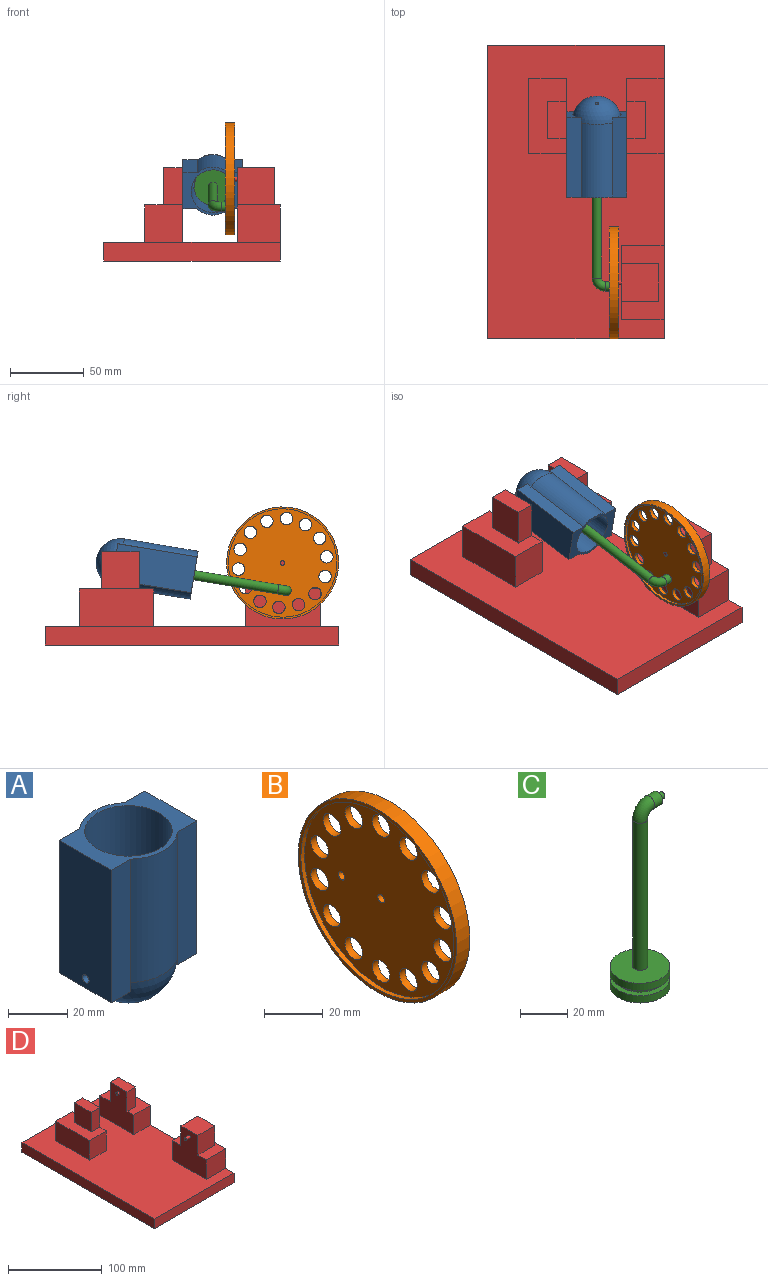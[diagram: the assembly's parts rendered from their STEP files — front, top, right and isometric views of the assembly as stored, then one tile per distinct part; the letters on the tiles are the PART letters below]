
ASSEMBLY  parts=4 mates=7
PART A: 22 faces, bbox 40.6x33x67.3 mm
  f0: sphere r=16.48mm, area 1697.5mm2, adj f2,f3,f6,f11,f20,f21
  f1: sphere r=14.7mm, area 1348.6mm2, adj f5,f20,f21
  f2: cylinder r=16.48mm len=50.8mm, axis (0,0,1), area 1242.1mm2, adj f0,f4,f8,f14
  f3: cylinder r=16.48mm len=50.8mm, axis (0,0,1), area 1178mm2, adj f0,f4,f7,f12
  f4: plane 40.63x32.95mm, normal (0,0,1), area 448.5mm2, adj f2,f3,f5,f7,f8,f9,f12,f13
  f5: cylinder r=14.7mm len=50.8mm, axis (0,0,1), area 4691.4mm2, adj f1,f4
  f6: cylinder r=16.48mm len=24.71mm, axis (0,0,1), area 106.5mm2, adj f0,f7,f8,f10
  f7: plane 54.61x9.65mm, normal (0,1,0), area 527.2mm2, adj f3,f4,f6,f9,f10
  f8: plane 54.61x9.18mm, normal (0,-1,0), area 501.4mm2, adj f2,f4,f6,f9,f10
  f9: plane 54.61x24.71mm, normal (1,0,0), area 1341.3mm2, adj f4,f7,f8,f10,f16
  f10: plane 24.71x9.65mm, normal (0,0,-1), area 137.2mm2, adj f6,f7,f8,f9
  f11: cylinder r=16.48mm len=24.71mm, axis (0,0,1), area 106.5mm2, adj f0,f12,f14,f15
  f12: plane 54.61x9.65mm, normal (0,1,0), area 527.2mm2, adj f3,f4,f11,f13,f15
  f13: plane 54.61x24.71mm, normal (-1,0,0), area 1341.4mm2, adj f4,f12,f14,f15,f18
  f14: plane 54.61x9.18mm, normal (0,-1,0), area 501.4mm2, adj f2,f4,f11,f13,f15
  f15: plane 24.71x9.65mm, normal (0,0,-1), area 137.2mm2, adj f11,f12,f13,f14
  f16: cylinder r=1.58mm len=3.17mm, axis (1,0,0), area 25.3mm2, adj f9,f17
  f17: plane 3.17x3.17mm, normal (1,0,0), area 7.9mm2, adj f16
  f18: cylinder r=1.58mm len=3.17mm, axis (-1,0,0), area 25.3mm2, adj f13,f19
  f19: plane 3.17x3.17mm, normal (-1,0,0), area 7.9mm2, adj f18
  f20: cylinder r=1.02mm len=4.01mm, axis (0,0,1), area 14.8mm2, adj f0,f1
  f21: cylinder r=1.02mm len=4.01mm, axis (0,0,1), area 14.8mm2, adj f0,f1
PART B: 23 faces, bbox 6.4x76.2x76.2 mm
  f0: plane 73.66x73.66mm, normal (1,0,0), area 3452.1mm2, adj f5,f7,f8,f9,f10,f11,f12,f13
  f1: plane 73.66x73.66mm, normal (-1,0,0), area 3452.1mm2, adj f6,f7,f8,f9,f10,f11,f12,f13
  f2: cylinder r=38.1mm len=76.2mm, axis (-1,0,0), area 1520.1mm2, adj f3,f4
  f3: plane 76.2x76.2mm, normal (1,0,0), area 299mm2, adj f2,f5
  f4: plane 76.2x76.2mm, normal (-1,0,0), area 299mm2, adj f2,f6
  f5: cylinder r=36.83mm len=73.66mm, axis (1,0,0), area 411.4mm2, adj f0,f3
  f6: cylinder r=36.83mm len=73.66mm, axis (-1,0,0), area 411.4mm2, adj f1,f4
  f7: cylinder r=1.59mm len=3.18mm, axis (1,0,0), area 27.9mm2, adj f0,f1
  f8: cylinder r=1.59mm len=3.18mm, axis (1,0,0), area 27.9mm2, adj f0,f1
  f9: cylinder r=4.25mm len=8.49mm, axis (1,0,0), area 74.6mm2, adj f0,f1
  f10: cylinder r=4.25mm len=8.49mm, axis (1,0,0), area 74.6mm2, adj f0,f1
  f11: cylinder r=4.25mm len=8.49mm, axis (1,0,0), area 74.6mm2, adj f0,f1
  f12: cylinder r=4.25mm len=8.49mm, axis (1,0,0), area 74.6mm2, adj f0,f1
  f13: cylinder r=4.25mm len=8.49mm, axis (1,0,0), area 74.6mm2, adj f0,f1
  f14: cylinder r=4.25mm len=8.49mm, axis (1,0,0), area 74.6mm2, adj f0,f1
  f15: cylinder r=4.25mm len=8.49mm, axis (1,0,0), area 74.6mm2, adj f0,f1
  f16: cylinder r=4.25mm len=8.49mm, axis (1,0,0), area 74.6mm2, adj f0,f1
  f17: cylinder r=4.25mm len=8.49mm, axis (1,0,0), area 74.6mm2, adj f0,f1
  f18: cylinder r=4.25mm len=8.49mm, axis (1,0,0), area 74.6mm2, adj f0,f1
  f19: cylinder r=4.25mm len=8.49mm, axis (1,0,0), area 74.6mm2, adj f0,f1
  f20: cylinder r=4.25mm len=8.49mm, axis (1,0,0), area 74.6mm2, adj f0,f1
  f21: cylinder r=4.25mm len=8.49mm, axis (1,0,0), area 74.6mm2, adj f0,f1
  f22: cylinder r=4.25mm len=8.49mm, axis (1,0,0), area 74.6mm2, adj f0,f1
PART C: 13 faces, bbox 26.1x25.4x96 mm
  f0: cylinder r=12.7mm len=25.4mm, axis (0,0,-1), area 304mm2, adj f1,f2
  f1: plane 25.4x25.4mm, normal (0,0,1), area 182.4mm2, adj f0,f3
  f2: plane 25.4x25.4mm, normal (0,0,-1), area 506.7mm2, adj f0
  f3: cylinder r=10.16mm len=20.32mm, axis (0,0,-1), area 162.1mm2, adj f1,f6
  f4: cylinder r=12.7mm len=25.4mm, axis (0,0,-1), area 304mm2, adj f5,f6
  f5: plane 25.4x25.4mm, normal (0,0,1), area 475mm2, adj f4,f7
  f6: plane 25.4x25.4mm, normal (0,0,-1), area 182.4mm2, adj f3,f4
  f7: cylinder r=3.17mm len=76.2mm, axis (0,0,-1), area 1520.1mm2, adj f5,f8
  f8: torus R=5.74mm, axis (0,-1,0), area 179.9mm2, adj f7,f9
  f9: cylinder r=3.17mm len=6.35mm, axis (-1,0,0), area 94.8mm2, adj f8,f10
  f10: plane 6.35x6.35mm, normal (1,0,0), area 23.8mm2, adj f9,f12
  f11: plane 3.18x3.18mm, normal (1,0,0), area 7.9mm2, adj f12
  f12: cylinder r=1.59mm len=3.18mm, axis (-1,0,0), area 28.6mm2, adj f10,f11
PART D: 37 faces, bbox 119.7x199.5x63.5 mm
  f0: plane 50.8x29.11mm, normal (0,0,1), area 833.5mm2, adj f7,f28,f29,f30,f31,f32,f34
  f1: plane 199.45x119.74mm, normal (0,0,1), area 19823.5mm2, adj f4,f5,f6,f7,f9,f10,f11,f12
  f2: plane 50.8x25.4mm, normal (0,0,1), area 967.7mm2, adj f7,f9,f10,f11,f20,f21,f22
  f3: plane 50.8x25.4mm, normal (0,0,1), area 967.7mm2, adj f12,f13,f14,f15,f16,f17,f18
  f4: plane 119.74x12.7mm, normal (0,1,0), area 1520.7mm2, adj f1,f5,f7,f8
  f5: plane 199.45x12.7mm, normal (-1,0,0), area 2533mm2, adj f1,f4,f6,f8
  f6: plane 119.74x12.7mm, normal (0,-1,0), area 1520.7mm2, adj f1,f5,f7,f8
  f7: plane 199.45x38.1mm, normal (1,0,0), area 5113.7mm2, adj f0,f1,f2,f4,f6,f8,f9,f11
  f8: plane 199.45x119.74mm, normal (0,0,-1), area 23882.8mm2, adj f4,f5,f6,f7
  f9: plane 25.4x25.4mm, normal (0,1,0), area 645.2mm2, adj f1,f2,f7,f10
  f10: plane 50.8x50.8mm, normal (-1,0,0), area 1927.6mm2, adj f1,f2,f9,f11,f20,f21,f23,f26
  f11: plane 25.4x25.4mm, normal (0,-1,0), area 645.2mm2, adj f1,f2,f7,f10
  f12: plane 25.4x25.4mm, normal (0,1,0), area 645.2mm2, adj f1,f3,f13,f15
  f13: plane 50.8x25.4mm, normal (-1,0,0), area 1290.3mm2, adj f1,f3,f12,f14
  f14: plane 25.4x25.4mm, normal (0,-1,0), area 645.2mm2, adj f1,f3,f13,f15
  f15: plane 50.8x50.8mm, normal (1,0,0), area 1927.6mm2, adj f1,f3,f12,f14,f16,f18,f19,f24
  f16: plane 25.4x12.7mm, normal (0,1,0), area 322.6mm2, adj f3,f15,f17,f19
  f17: plane 25.4x25.4mm, normal (-1,0,0), area 645.2mm2, adj f3,f16,f18,f19
  f18: plane 25.4x12.7mm, normal (0,-1,0), area 322.6mm2, adj f3,f15,f17,f19
  f19: plane 25.4x12.7mm, normal (0,0,1), area 322.6mm2, adj f15,f16,f17,f18
  f20: plane 25.4x12.7mm, normal (0,1,0), area 322.6mm2, adj f2,f10,f22,f23
  f21: plane 25.4x12.7mm, normal (0,-1,0), area 322.6mm2, adj f2,f10,f22,f23
  f22: plane 25.4x25.4mm, normal (1,0,0), area 645.2mm2, adj f2,f20,f21,f23
  f23: plane 25.4x12.7mm, normal (0,0,1), area 322.6mm2, adj f10,f20,f21,f22
  f24: cylinder r=1.59mm len=3.18mm, axis (-1,0,0), area 25.3mm2, adj f15,f25
  f25: plane 3.18x3.18mm, normal (1,0,0), area 7.9mm2, adj f24
  f26: cylinder r=1.59mm len=3.18mm, axis (1,0,0), area 25.3mm2, adj f10,f27
  f27: plane 3.18x3.18mm, normal (-1,0,0), area 7.9mm2, adj f26
  f28: plane 29.11x25.4mm, normal (0,1,0), area 739.3mm2, adj f0,f1,f7,f34
  f29: plane 29.11x25.4mm, normal (0,-1,0), area 739.3mm2, adj f0,f1,f7,f34
  f30: plane 25.4x25.4mm, normal (0,1,0), area 645.2mm2, adj f0,f32,f33,f34
  f31: plane 25.4x25.4mm, normal (0,-1,0), area 645.2mm2, adj f0,f32,f33,f34
  f32: plane 25.4x25.4mm, normal (1,0,0), area 645.2mm2, adj f0,f30,f31,f33
  f33: plane 25.4x25.4mm, normal (0,0,1), area 645.2mm2, adj f30,f31,f32,f34
  f34: plane 50.8x50.8mm, normal (-1,0,0), area 1927.6mm2, adj f0,f1,f28,f29,f30,f31,f33,f35
  f35: cylinder r=1.59mm len=6.35mm, axis (1,0,0), area 63.3mm2, adj f34,f36
  f36: plane 3.18x3.18mm, normal (-1,0,0), area 7.9mm2, adj f35
PLACE A rot(axis=(1,0,0),99.5deg) t=(4.73,-42.98,55.39)mm
PLACE B rot(axis=(-1,0,0),98deg) t=(13.21,-153.28,55.3)mm
PLACE C rot(axis=(1,0,0),99.5deg) t=(4.73,-65.08,51.68)mm
PLACE D t=(-23.27,-87.59,-0.49)mm fixed
MATE cylindrical B.f7 <-> D.f35  axis (1,0,0) through (14.99,-153.28,55.3)mm
MATE planar A.f9 <-> D.f26  axis (1,0,0) through (25.05,-66.32,51.69)mm
MATE parallel B.f5 <-> A.f13  axis (-1,0,0) through (14.99,-153.28,55.3)mm
MATE cylindrical A.f18 <-> D.f24  axis (-1,0,0) through (-15.58,-42.98,55.39)mm
MATE cylindrical B.f8 <-> C.f12  axis (1,0,0) through (17.78,-155.91,36.43)mm
MATE cylindrical C.f0 <-> A.f6  axis (0,-0.99,-0.17) through (4.73,-75.1,50)mm
MATE planar D.f35 <-> B.f1  axis (-1,0,0) through (14.99,-153.28,55.3)mm
